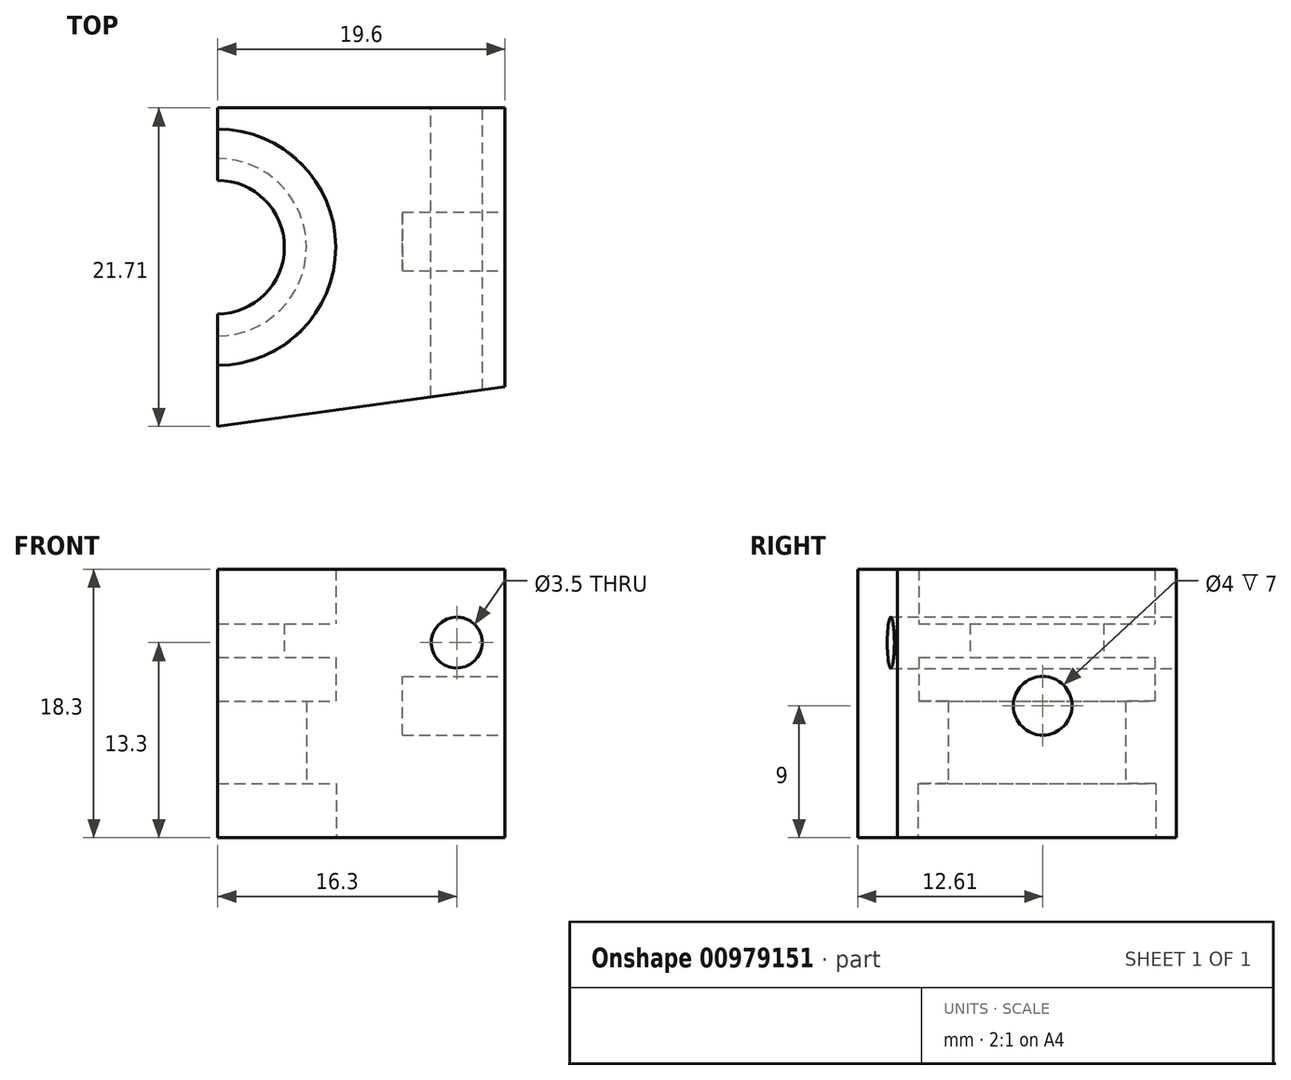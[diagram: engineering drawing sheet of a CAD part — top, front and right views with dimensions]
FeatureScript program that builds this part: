
annotation { "Feature Type Name" : "Feature", "Feature Type Description" : "" }
export const myFeature = defineFeature(function(context is Context, id is Id, definition is map)
    precondition{}
    {
        {
            var Q0;
            Q0=qCreatedBy(makeId("Top.planeOp"),FACE);
            var sketch = newSketch(context, id + "F0", { "sketchPlane" : qUnion([Q0])});
            skLineSegment(sketch, "E0", {"start": v(0, 12.21) * mm, "end": v(19.6, 9.5) * mm});
            skLineSegment(sketch, "E1", {"start": v(19.6, 9.5) * mm, "end": v(19.6, 0) * mm});
            skLineSegment(sketch, "E2", {"start": v(0, 12.21) * mm, "end": v(0, 0) * mm, "construction": true});
            skArc(sketch, "E3", {"start": v(8.1, 0) * mm, "mid": v(5.73, 5.73) * mm, "end": v(0, 8.1) * mm});
            skLineSegment(sketch, "E4", {"start": v(0, 12.21) * mm, "end": v(0, 8.1) * mm});
            skLineSegment(sketch, "E5.MirrorCS", {"start": v(0, -12.21) * mm, "end": v(0, -8.1) * mm});
            skLineSegment(sketch, "E6.MirrorCS", {"start": v(0, -12.21) * mm, "end": v(0, 0) * mm, "construction": true});
            skLineSegment(sketch, "E7.MirrorCS", {"start": v(0, -12.21) * mm, "end": v(19.6, -9.5) * mm});
            skLineSegment(sketch, "E8.MirrorCS", {"start": v(19.6, -9.5) * mm, "end": v(19.6, 0) * mm});
            skArc(sketch, "E9.MirrorCS", {"start": v(8.1, 0) * mm, "mid": v(5.73, -5.73) * mm, "end": v(0, -8.1) * mm});
            skSolve(sketch);
        }
        {
            var Q0;
            Q0=makeQuery(id+"F0.imprint","IMPRINT",FACE,{"disambiguationData":[TD([[makeQuery(id+"F0.imprint","IMPRINT",EDGE,{"derivedFrom":sQuery(id+"F0.wireOp",EDGE,"E0")}),-1.0]])]});
            extrude(context, id + "F1", {"entities" : qUnion([Q0]), "depth" : 3.7 * mm, "offsetDistance" : 25 * mm});
        }
        {
            var Q0;
            Q0=makeQuery(id+"F1.opExtrude","CAP_FACE",FACE,{"disambiguationData":[OSD([sQuery(id+"F0.wireOp",EDGE,"E0"),sQuery(id+"F0.wireOp",EDGE,"E1"),sQuery(id+"F0.wireOp",EDGE,"E3"),sQuery(id+"F0.wireOp",EDGE,"E4"),sQuery(id+"F0.wireOp",EDGE,"E5.MirrorCS"),sQuery(id+"F0.wireOp",EDGE,"E7.MirrorCS"),sQuery(id+"F0.wireOp",EDGE,"E8.MirrorCS"),sQuery(id+"F0.wireOp",EDGE,"E9.MirrorCS")])],"isStart":false});
            var sketch = newSketch(context, id + "F2", { "sketchPlane" : qUnion([Q0])});
            skArc(sketch, "E10", {"start": v(0, -6.05) * mm, "mid": v(6.05, 0) * mm, "end": v(0, 6.05) * mm});
            skLineSegment(sketch, "E11", {"start": v(0, 8.1) * mm, "end": v(0, 6.05) * mm});
            skLineSegment(sketch, "E12.trimOffspring", {"start": v(0, -6.05) * mm, "end": v(0, -8.1) * mm});
            skLineSegment(sketch, "E13", {"start": v(0, -8.1) * mm, "end": v(0, -12.21) * mm});
            skLineSegment(sketch, "E14", {"start": v(0, -12.2) * mm, "end": v(19.6, -9.5) * mm});
            skLineSegment(sketch, "E15", {"start": v(19.6, -9.5) * mm, "end": v(19.6, 9.5) * mm});
            skLineSegment(sketch, "E16", {"start": v(19.6, 9.5) * mm, "end": v(0, 12.2) * mm});
            skLineSegment(sketch, "E17", {"start": v(0, 12.21) * mm, "end": v(0, 8.1) * mm});
            skSolve(sketch);
        }
        {
            var Q0;
            Q0 = qSketchRegion(id + "F2", true);
            extrude(context, id + "F3", {"entities" : qUnion([Q0]), "operationType" : NewBodyOperationType.ADD, "depth" : 5.6 * mm, "offsetDistance" : 25 * mm});
        }
        {
            var Q0;
            Q0=makeQuery(id+"F3.opExtrude","CAP_FACE",FACE,{"disambiguationData":[OSD([sQuery(id+"F2.wireOp",EDGE,"E10"),sQuery(id+"F2.wireOp",EDGE,"E11"),sQuery(id+"F2.wireOp",EDGE,"E12.trimOffspring"),sQuery(id+"F2.wireOp",EDGE,"E13"),sQuery(id+"F2.wireOp",EDGE,"E14"),sQuery(id+"F2.wireOp",EDGE,"E15"),sQuery(id+"F2.wireOp",EDGE,"E16"),sQuery(id+"F2.wireOp",EDGE,"E17")])],"isStart":false});
            var sketch = newSketch(context, id + "F4", { "sketchPlane" : qUnion([Q0])});
            skArc(sketch, "E18", {"start": v(0, -8.05) * mm, "mid": v(8.05, 0) * mm, "end": v(0, 8.05) * mm});
            skLineSegment(sketch, "E19", {"start": v(0, 8.05) * mm, "end": v(0, 12.21) * mm});
            skLineSegment(sketch, "E20", {"start": v(0, 12.2) * mm, "end": v(19.6, 9.5) * mm});
            skLineSegment(sketch, "E21", {"start": v(19.6, 9.5) * mm, "end": v(19.6, -9.5) * mm});
            skLineSegment(sketch, "E22", {"start": v(19.6, -9.5) * mm, "end": v(0, -12.2) * mm});
            skLineSegment(sketch, "E23", {"start": v(0, -12.21) * mm, "end": v(0, -8.05) * mm});
            skSolve(sketch);
        }
        {
            var Q0;
            Q0 = qSketchRegion(id + "F4", true);
            extrude(context, id + "F5", {"entities" : qUnion([Q0]), "operationType" : NewBodyOperationType.ADD, "depth" : 3 * mm, "offsetDistance" : 25 * mm});
        }
        {
            var Q0;
            Q0=makeQuery(id+"F5.opExtrude","CAP_FACE",FACE,{"disambiguationData":[OSD([sQuery(id+"F4.wireOp",EDGE,"E18"),sQuery(id+"F4.wireOp",EDGE,"E19"),sQuery(id+"F4.wireOp",EDGE,"E20"),sQuery(id+"F4.wireOp",EDGE,"E21"),sQuery(id+"F4.wireOp",EDGE,"E22"),sQuery(id+"F4.wireOp",EDGE,"E23")])],"isStart":false});
            var sketch = newSketch(context, id + "F6", { "sketchPlane" : qUnion([Q0])});
            skArc(sketch, "E24", {"start": v(0, -4.55) * mm, "mid": v(4.55, 0) * mm, "end": v(0, 4.55) * mm});
            skLineSegment(sketch, "E25", {"start": v(0, 4.55) * mm, "end": v(0, 12.21) * mm});
            skLineSegment(sketch, "E26", {"start": v(0, 12.2) * mm, "end": v(19.6, 9.5) * mm});
            skLineSegment(sketch, "E27", {"start": v(19.6, 9.5) * mm, "end": v(19.6, -9.5) * mm});
            skLineSegment(sketch, "E28", {"start": v(19.6, -9.5) * mm, "end": v(0, -12.2) * mm});
            skLineSegment(sketch, "E29", {"start": v(0, -12.21) * mm, "end": v(0, -4.55) * mm});
            skSolve(sketch);
        }
        {
            var Q0;
            Q0 = qSketchRegion(id + "F6", true);
            extrude(context, id + "F7", {"entities" : qUnion([Q0]), "operationType" : NewBodyOperationType.ADD, "depth" : 2.3 * mm, "offsetDistance" : 25 * mm});
        }
        {
            var Q0;
            Q0=makeQuery(id+"F7.opExtrude","CAP_FACE",FACE,{"disambiguationData":[OSD([sQuery(id+"F6.wireOp",EDGE,"E24"),sQuery(id+"F6.wireOp",EDGE,"E25"),sQuery(id+"F6.wireOp",EDGE,"E26"),sQuery(id+"F6.wireOp",EDGE,"E27"),sQuery(id+"F6.wireOp",EDGE,"E28"),sQuery(id+"F6.wireOp",EDGE,"E29")])],"isStart":false});
            var sketch = newSketch(context, id + "F8", { "sketchPlane" : qUnion([Q0])});
            skArc(sketch, "E30", {"start": v(0, -8.05) * mm, "mid": v(8.05, 0) * mm, "end": v(0, 8.05) * mm});
            skLineSegment(sketch, "E31", {"start": v(0, 8.05) * mm, "end": v(0, 12.21) * mm});
            skLineSegment(sketch, "E32", {"start": v(0, 12.2) * mm, "end": v(19.6, 9.5) * mm});
            skLineSegment(sketch, "E33", {"start": v(19.6, 9.5) * mm, "end": v(19.6, -9.5) * mm});
            skLineSegment(sketch, "E34", {"start": v(19.6, -9.5) * mm, "end": v(0, -12.2) * mm});
            skLineSegment(sketch, "E35", {"start": v(0, -12.21) * mm, "end": v(0, -8.05) * mm});
            skSolve(sketch);
        }
        {
            var Q0;
            Q0 = qSketchRegion(id + "F8", true);
            extrude(context, id + "F9", {"entities" : qUnion([Q0]), "operationType" : NewBodyOperationType.ADD, "depth" : 3.7 * mm, "offsetDistance" : 25 * mm});
        }
        {
            var Q0;
            Q0=makeQuery(id+"F1.opExtrude","CAP_FACE",FACE,{"disambiguationData":[OSD([sQuery(id+"F0.wireOp",EDGE,"E0"),sQuery(id+"F0.wireOp",EDGE,"E1"),sQuery(id+"F0.wireOp",EDGE,"E3"),sQuery(id+"F0.wireOp",EDGE,"E4"),sQuery(id+"F0.wireOp",EDGE,"E5.MirrorCS"),sQuery(id+"F0.wireOp",EDGE,"E7.MirrorCS"),sQuery(id+"F0.wireOp",EDGE,"E8.MirrorCS"),sQuery(id+"F0.wireOp",EDGE,"E9.MirrorCS")])],"isStart":true});
            var sketch = newSketch(context, id + "F10", { "sketchPlane" : qUnion([Q0])});
            skLineSegment(sketch, "E36", {"start": v(19.6, -9.5) * mm, "end": v(0, -9.5) * mm});
            skLineSegment(sketch, "E37", {"start": v(0, -9.5) * mm, "end": v(0, -12.21) * mm});
            skLineSegment(sketch, "E38", {"start": v(0, -12.2) * mm, "end": v(19.6, -9.5) * mm});
            skSolve(sketch);
        }
        {
            var Q0;
            Q0 = qSketchRegion(id + "F10", true);
            extrude(context, id + "F11", {"entities" : qUnion([Q0]), "operationType" : NewBodyOperationType.REMOVE, "oppositeDirection" : true, "depth" : 25 * mm, "offsetDistance" : 25 * mm, "hasSecondDirection" : true, "secondDirectionOppositeDirection" : false, "secondDirectionDepth" : 25 * mm});
        }
        {
            var Q0;
            Q0=makeQuery(id+"F9.boolean.opBoolean","MERGE",FACE,{"derivedFrom":[makeQuery(id+"F7.boolean.opBoolean","MERGE",FACE,{"derivedFrom":[makeQuery(id+"F5.boolean.opBoolean","MERGE",FACE,{"derivedFrom":[makeQuery(id+"F3.boolean.opBoolean","MERGE",FACE,{"derivedFrom":[makeQuery(id+"F1.opExtrude","SWEPT_FACE",FACE,{"disambiguationData":[OSD([sQuery(id+"F0.wireOp",EDGE,"E1"),sQuery(id+"F0.wireOp",EDGE,"E8.MirrorCS")])]}),makeQuery(id+"F3.opExtrude","SWEPT_FACE",FACE,{"disambiguationData":[OSD([sQuery(id+"F2.wireOp",EDGE,"E15")])]})]}),makeQuery(id+"F5.opExtrude","SWEPT_FACE",FACE,{"disambiguationData":[OSD([sQuery(id+"F4.wireOp",EDGE,"E21")])]})]}),makeQuery(id+"F7.opExtrude","SWEPT_FACE",FACE,{"disambiguationData":[OSD([sQuery(id+"F6.wireOp",EDGE,"E27")])]})]}),makeQuery(id+"F9.opExtrude","SWEPT_FACE",FACE,{"disambiguationData":[OSD([sQuery(id+"F8.wireOp",EDGE,"E33")])]})]});
            var sketch = newSketch(context, id + "F12", { "sketchPlane" : qUnion([Q0])});
            skLineSegment(sketch, "E39", {"start": v(9.5, 9) * mm, "end": v(0.4, 9) * mm, "construction": true});
            skLineSegment(sketch, "E40", {"start": v(0.4, 9) * mm, "end": v(0.4, 18.3) * mm, "construction": true});
            skCircle(sketch, "E41", {"center": v(0.4, 9) * mm, "radius": 2 * mm});
            skSolve(sketch);
        }
        {
            var Q0;
            Q0 = qSketchRegion(id + "F12", true);
            extrude(context, id + "F13", {"entities" : qUnion([Q0]), "operationType" : NewBodyOperationType.REMOVE, "oppositeDirection" : true, "depth" : 7 * mm, "offsetDistance" : 25 * mm});
        }
        {
            var Q0;
            Q0=makeQuery(id+"F11.boolean.opBoolean","COPY",FACE,{"derivedFrom":makeQuery(id+"F11.opExtrude","SWEPT_FACE",FACE,{"disambiguationData":[OSD([sQuery(id+"F10.wireOp",EDGE,"E36")])]})});
            var sketch = newSketch(context, id + "F14", { "sketchPlane" : qUnion([Q0])});
            skLineSegment(sketch, "E42", {"start": v(-19.6, 13.3) * mm, "end": v(-16.3, 13.3) * mm, "construction": true});
            skLineSegment(sketch, "E43", {"start": v(-16.3, 13.3) * mm, "end": v(-16.3, 18.3) * mm, "construction": true});
            skCircle(sketch, "E44", {"center": v(-16.3, 13.3) * mm, "radius": 1.75 * mm});
            skSolve(sketch);
        }
        {
            var Q0;
            Q0 = qSketchRegion(id + "F14", true);
            extrude(context, id + "F15", {"entities" : qUnion([Q0]), "operationType" : NewBodyOperationType.REMOVE, "oppositeDirection" : true, "depth" : 25 * mm, "offsetDistance" : 25 * mm});
        }
    });
